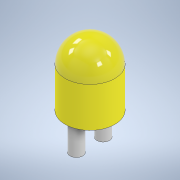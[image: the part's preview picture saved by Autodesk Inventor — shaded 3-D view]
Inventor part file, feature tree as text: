
AUTODESK INVENTOR PART (.ipt)
format: ipt  version: 2021 (Build 250183000, 183)  size: 127,488 bytes
history: native  units: mm
features: sketch x3, extrude x2, revolve x1
ambient origin geometry x8: Origin, YZ Plane, XZ Plane, XY Plane, X Axis, Y Axis, Z Axis, Center Point
bodies: Solid1 (feature_tree)
feature tree (6):
  revolve  "Revolution1"  Angle=180.0deg
  extrude  "Extrusion1"  Depth=30.0mm TaperAngle=0.0deg
  extrude  "Extrusion2"  [1 undecoded]
  sketch  "Sketch1"  dims[d0=50.0mm d1=180.0deg]
  sketch  "Sketch2"  dims[d2=40.0mm d3=0.0mm d4=30.0mm d5=0.0mm]
  sketch  "Sketch3"
note: 1 required parameter value undecoded (feature->parameter linkage not recoverable at this tier; creation-order binding heuristic only, values carry confidence <= 0.55)
